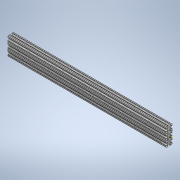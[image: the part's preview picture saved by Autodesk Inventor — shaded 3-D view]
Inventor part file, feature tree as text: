
AUTODESK INVENTOR PART (.ipt)
format: ipt  version: 2020 (Build 240168000, 168)  size: 378,880 bytes
history: native  units: in
note: dims shown in document units (in); Inventor stores cm internally (conversion verified against a paired STEP export)
features: sketch x2, extrude x1
ambient origin geometry x8: Origin, YZ Plane, XZ Plane, XY Plane, X Axis, Y Axis, Z Axis, Center Point
bodies: Solid1 (feature_tree)
feature tree (3):
  extrude  "Extrusion1"  [1 undecoded]
  sketch  "Sketch2"
  sketch  "Sketch1"  dims[d0=26.0in d1=0.0in]
note: 1 required parameter value undecoded (feature->parameter linkage not recoverable at this tier; creation-order binding heuristic only, values carry confidence <= 0.55)
